# Revit family: LUXI_WATERPROOF LIGHT_HR
name_source: partatom
category: Apparecchi per illuminazione
revit_build: Autodesk Revit 2016 (Build: 20161004_0715(x64)
units: mm (PartAtom-declared; Revit-internal decimal feet)

## family parameters
Condiviso = No
Host = Superficie
Numero OmniClass = 23.80.70.00
Punto di calcolo locali = Sì
Quota connettore circolare = Usa diametro
Sorgente d'illuminazione = Sì
Taglio con vuoti quando caricato = No
Tipo di parte = Normale
Titolo OmniClass = Lighting

## types (2) — shared parameters
Angolo inclinazione = -90.00°
CRI = ≥80 (typ.)
Carico apparente = 80 VA
Certifications = CE / RohS
Color = Black
Descrizione = Waterproof ceiling
Dust and water protection rating = IP 69K
Emetti da larghezza rettangolo = 81 mm  [stored 0.265748 ft]
Emetti da lunghezza rettangolo = 1450 mm  [stored 4.75722 ft]
Energy class = A+
File diagramma fotometrico = WPHR080150BG840K Luxi SERIE HR 80W 4000K.IES
Filtro dei colori = 16777215
H = 78 mm  [stored 0.255906 ft]
IFCExportAs = IfcLightFixtureType
Impact rating = IK10 (20 Joule)
Installation = Suspended / ceiling
Lenght = 1490 mm  [stored 4.88845 ft]
Lifetime = L70B20 50.000h
Light distribution = Downlight
Light source = LED SMD
Masterformat 2016 code = 26.50.00
Masterformat 2016 description = Lighting
Material 1 = Steel INOX 316_Black
Material 3 = Steel_Black
Modello = HR Series | Waterproof Light
Operating temperature = -40°C / +45°C
Optics = Diffuser
Photobiological risk group = RG0
Power factor = ≥0,95 (typ.)
Power supply = Included
Produttore = Luxi Illuminazione S.r.l.
Prospetto di default = 2000 mm  [stored 6.56168 ft]
Protection class = I
Rated supply voltage = 220-240V AC / 50-60 Hz
Rendi la forma visibile nel rendering = No
Review = 3
Size = 1490x78x96
Step MacAdam (SDCM) = <4
URL = https://www.luxi.lighting
Uniclass 2015 code = EF_70_80
Uniclass 2015 description = Lighting
Variazione temperatura colore lampada con luminosità attenuata = <Nessuno>
Warranty = 3 years
Wattage = 80 W
Weight = 4.50 kg
Width = 96 mm  [stored 0.314961 ft]

## per-type parameters (varying)
| type | Material 2 |
| WPHR080150BG840K | Tempered Glass |
| WPHR080150BP840K | PMMA Acrylic |

note: column(s) folded — value = type name in every type: Code

note: [stored X ft] marks values corroborated as IEEE doubles in the binary element streams (Revit-internal decimal feet)
